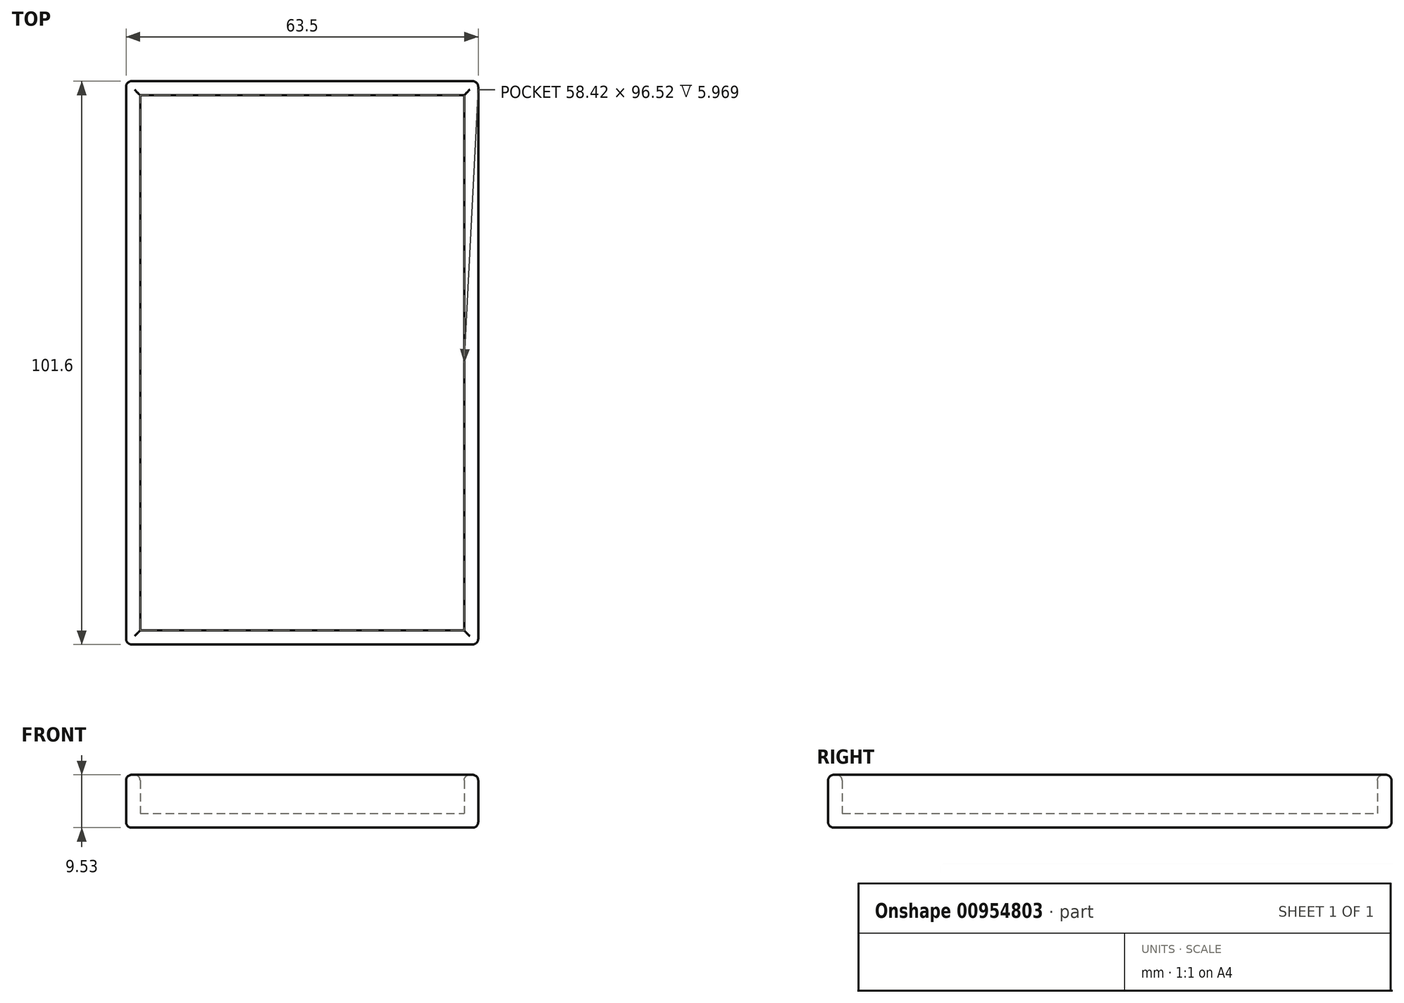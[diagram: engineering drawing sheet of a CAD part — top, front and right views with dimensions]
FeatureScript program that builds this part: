
annotation { "Feature Type Name" : "Feature", "Feature Type Description" : "" }
export const myFeature = defineFeature(function(context is Context, id is Id, definition is map)
    precondition{}
    {
        {
            var Q0;
            Q0=qCreatedBy(makeId("Top.planeOp"),FACE);
            var sketch = newSketch(context, id + "F0", { "sketchPlane" : qUnion([Q0])});
            skLineSegment(sketch, "E0.bottom", {"start": v(-31.75, -50.8) * mm, "end": v(31.75, -50.8) * mm});
            skLineSegment(sketch, "E0.top", {"start": v(-31.75, 50.8) * mm, "end": v(31.75, 50.8) * mm});
            skLineSegment(sketch, "E0.left", {"start": v(-31.75, -50.8) * mm, "end": v(-31.75, 50.8) * mm});
            skLineSegment(sketch, "E0.right", {"start": v(31.75, -50.8) * mm, "end": v(31.75, 50.8) * mm});
            skPoint(sketch, "E0.middle", {"position": v(0, 0) * mm});
            skSolve(sketch);
        }
        {
            var Q0;
            Q0 = qSketchRegion(id + "F0", true);
            extrude(context, id + "F1", {"entities" : qUnion([Q0]), "depth" : 9.52 * mm, "offsetDistance" : 25.4 * mm});
        }
        {
            var Q0;
            Q0=makeQuery(id+"F1.opExtrude","CAP_FACE",FACE,{"disambiguationData":[OSD([sQuery(id+"F0.wireOp",EDGE,"E0.bottom"),sQuery(id+"F0.wireOp",EDGE,"E0.top"),sQuery(id+"F0.wireOp",EDGE,"E0.left"),sQuery(id+"F0.wireOp",EDGE,"E0.right")])],"isStart":false});
            shell(context, id + "F2", {"entities" : qUnion([Q0]), "thickness" : 2.54 * mm});
        }
        {
            var Q0;
            Q0=makeQuery(id+"F1.opExtrude","CAP_FACE",FACE,{"disambiguationData":[OSD([sQuery(id+"F0.wireOp",EDGE,"E0.bottom"),sQuery(id+"F0.wireOp",EDGE,"E0.top"),sQuery(id+"F0.wireOp",EDGE,"E0.left"),sQuery(id+"F0.wireOp",EDGE,"E0.right")])],"isStart":true});
            var Q1;
            Q1=makeQuery(id+"F1.opExtrude","CAP_FACE",FACE,{"disambiguationData":[OSD([sQuery(id+"F0.wireOp",EDGE,"E0.bottom"),sQuery(id+"F0.wireOp",EDGE,"E0.top"),sQuery(id+"F0.wireOp",EDGE,"E0.left"),sQuery(id+"F0.wireOp",EDGE,"E0.right")])],"isStart":false});
            var Q2;
            Q2=makeQuery(id+"F1.opExtrude","SWEPT_FACE",FACE,{"disambiguationData":[OSD([sQuery(id+"F0.wireOp",EDGE,"E0.left")])]});
            var Q3;
            Q3=makeQuery(id+"F1.opExtrude","SWEPT_FACE",FACE,{"disambiguationData":[OSD([sQuery(id+"F0.wireOp",EDGE,"E0.top")])]});
            var Q4;
            Q4=makeQuery(id+"F1.opExtrude","SWEPT_FACE",FACE,{"disambiguationData":[OSD([sQuery(id+"F0.wireOp",EDGE,"E0.right")])]});
            var Q5;
            Q5=makeQuery(id+"F1.opExtrude","SWEPT_FACE",FACE,{"disambiguationData":[OSD([sQuery(id+"F0.wireOp",EDGE,"E0.bottom")])]});
            fillet(context, id + "F3", {"entities" : qUnion([Q0, Q1, Q2, Q3, Q4, Q5]), "radius" : 1.02 * mm, "tangentPropagation" : true, "allowEdgeOverflow" : false});
        }
    });
